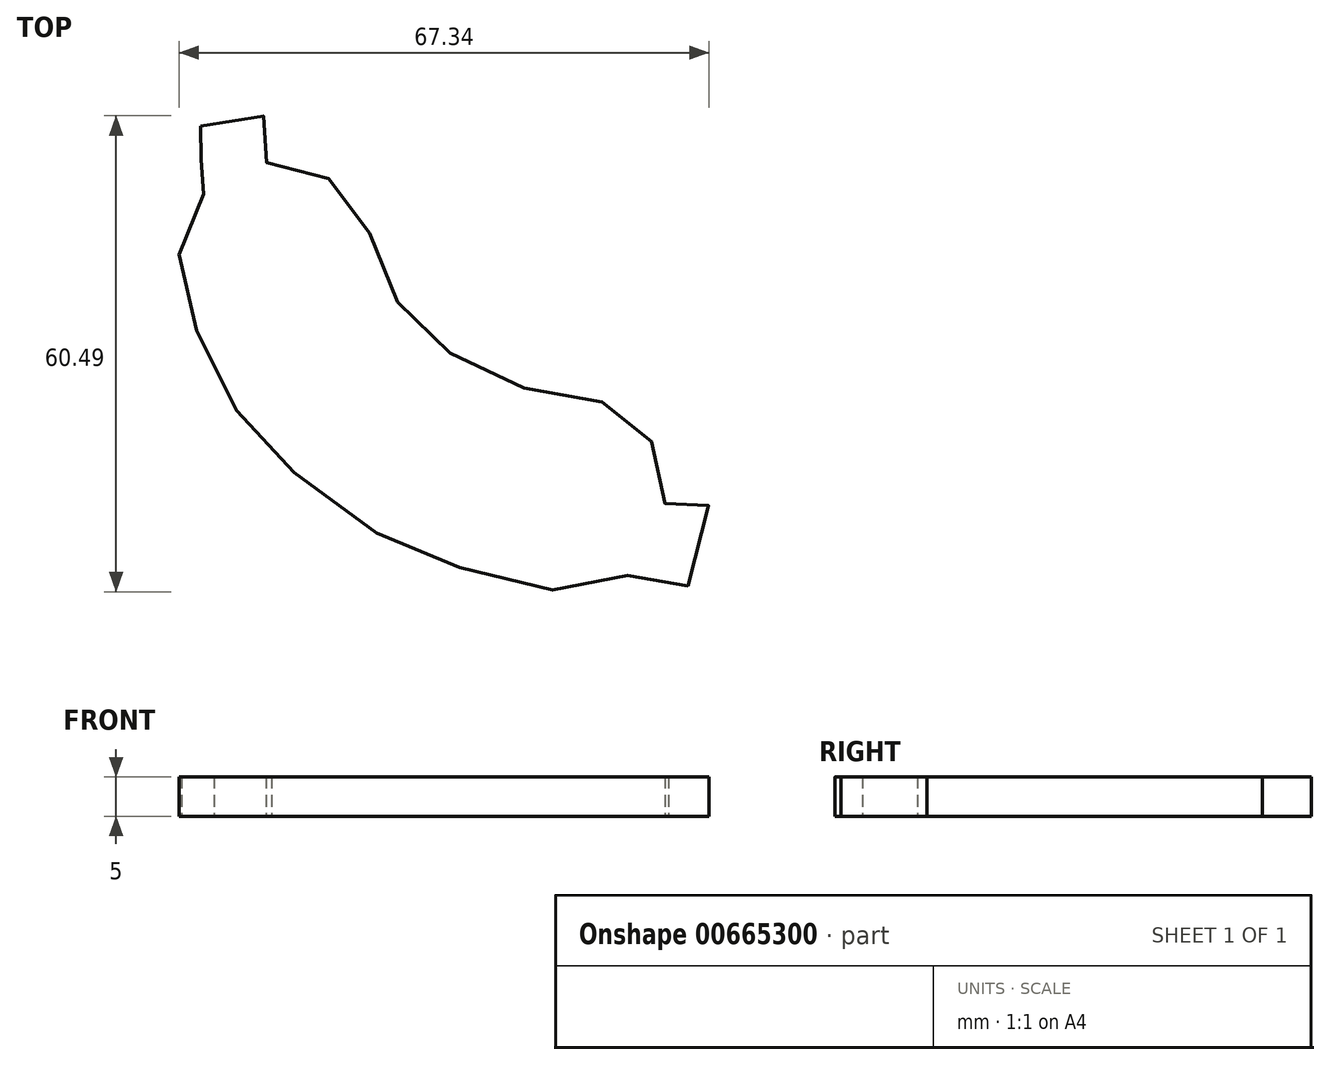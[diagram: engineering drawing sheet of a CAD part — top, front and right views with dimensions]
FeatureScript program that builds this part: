
annotation { "Feature Type Name" : "Feature", "Feature Type Description" : "" }
export const myFeature = defineFeature(function(context is Context, id is Id, definition is map)
    precondition{}
    {
        {
            var Q0;
            Q0=qCreatedBy(makeId("Top.planeOp"),FACE);
            var sketch = newSketch(context, id + "F0", { "sketchPlane" : qUnion([Q0])});
            skFitSpline(sketch, "E0", {"points": [v(-67.95, 63.84) * mm, v(-70.38, 62.72) * mm, v(-68.14, 59.91) * mm, v(-67.02, 57.86) * mm, v(-66.27, 56.92) * mm, v(-68.33, 54.5) * mm, v(-70.38, 50.38) * mm, v(-70.38, 43.46) * mm, v(-67.95, 36.73) * mm, v(-63.65, 28.13) * mm, v(-59.35, 22.9) * mm, v(-49.63, 14.67) * mm, v(-41.4, 10.19) * mm, v(-31.87, 6.82) * mm, v(-21.78, 4.77) * mm, v(-14.86, 5.89) * mm, v(-10.94, 8.13) * mm, v(-5.7, 5.51) * mm, v(-3.65, 14.67) * mm, v(-3.65, 16.36) * mm, v(-8.7, 15.24) * mm, v(-8.5, 18.6) * mm, v(-10.38, 23.27) * mm, v(-13.18, 26.83) * mm, v(-18.04, 29.07) * mm, v(-25.14, 30.2) * mm, v(-32.8, 32.8) * mm, v(-38.6, 36.92) * mm, v(-42.72, 41.22) * mm, v(-45.52, 47.2) * mm, v(-47.39, 52.62) * mm, v(-50.94, 56.74) * mm, v(-57.86, 58.98) * mm, v(-59.54, 59.17) * mm, v(-59.17, 62.9) * mm, v(-59.35, 64.96) * mm, v(-64.59, 64.59) * mm, v(-67.95, 63.84) * mm]});
            skSolve(sketch);
        }
        {
            var Q0;
            Q0 = qSketchRegion(id + "F0", true);
            extrude(context, id + "F1", {"entities" : qUnion([Q0]), "depth" : 5 * mm, "offsetDistance" : 25.4 * mm});
        }
    });
